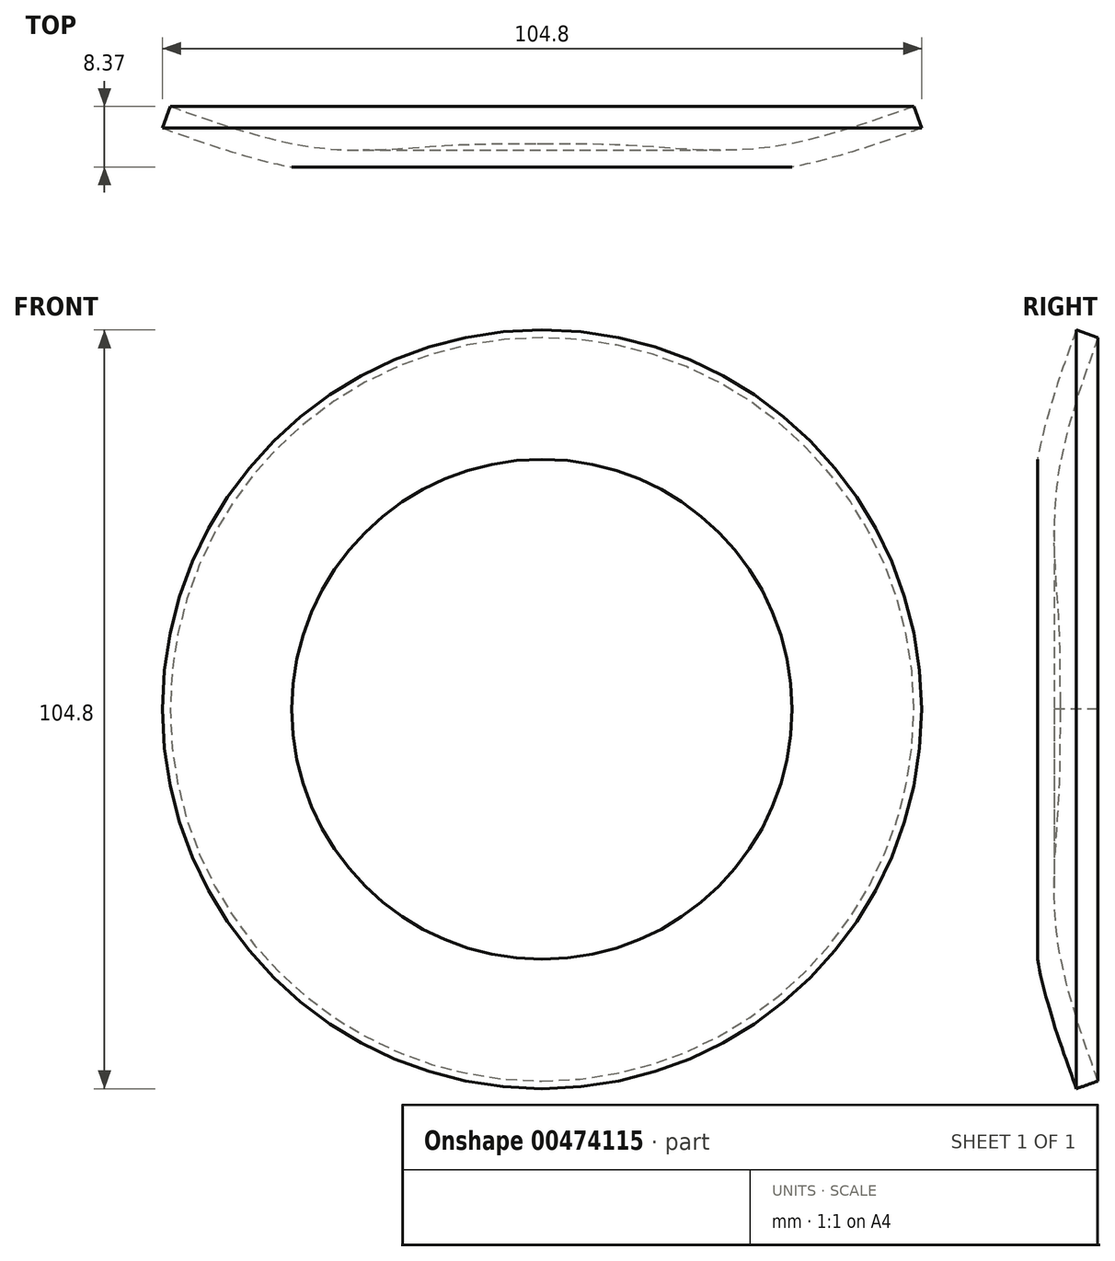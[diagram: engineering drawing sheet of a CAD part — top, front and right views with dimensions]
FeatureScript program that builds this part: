
annotation { "Feature Type Name" : "Feature", "Feature Type Description" : "" }
export const myFeature = defineFeature(function(context is Context, id is Id, definition is map)
    precondition{}
    {
        {
            var Q0;
            Q0=qCreatedBy(makeId("Top.planeOp"),FACE);
            var sketch = newSketch(context, id + "F0", { "sketchPlane" : qUnion([Q0])});
            skLineSegment(sketch, "E0", {"start": v(-26.85, 0) * mm, "end": v(-26.85, 3.18) * mm});
            skFitSpline(sketch, "E1", {"points": [v(24.49, 8.37) * mm, v(3.65, 2.62) * mm, v(-13.57, 2.91) * mm, v(-26.85, 3.18) * mm], "startDerivative": vector(-56.48, -19.98) * mm, "endDerivative": vector(-56.26, 0) * mm});
            skFitSpline(sketch, "E2.0", {"points": [v(25.55, 5.38) * mm, v(23.2, 4.55) * mm, v(19.66, 3.29) * mm, v(14.88, 1.77) * mm, v(11.27, 0.78) * mm, v(8.23, 0.1) * mm, v(5.78, -0.31) * mm, v(3.92, -0.56) * mm, v(2.07, -0.72) * mm, v(-0.36, -0.86) * mm, v(-3.34, -0.87) * mm, v(-6.76, -0.74) * mm, v(-9.98, -0.53) * mm, v(-12.46, -0.34) * mm, v(-14.28, -0.22) * mm, v(-16.02, -0.13) * mm, v(-18.12, -0.06) * mm, v(-20.7, -0.01) * mm, v(-23.52, 0) * mm, v(-25.68, 0) * mm, v(-26.85, 0) * mm]});
            skLineSegment(sketch, "E3", {"start": v(24.49, 8.37) * mm, "end": v(25.55, 5.38) * mm});
            skSolve(sketch);
        }
        {
            var Q0;
            Q0=makeQuery(id+"F0.imprint","IMPRINT",FACE,{"disambiguationData":[TD([[makeQuery(id+"F0.imprint","IMPRINT",EDGE,{"derivedFrom":sQuery(id+"F0.wireOp",EDGE,"E0")}),-1.0]])]});
            var Q1;
            Q1=sQuery(id+"F0.wireOp",EDGE,"E0");
            revolve(context, id + "F1", {"entities" : qUnion([Q0]), "axis" : qUnion([Q1]), "revolveType" : RevolveType.FULL});
        }
        {
            var Q0;
            Q0=qCreatedBy(makeId("Front.planeOp"),FACE);
            var sketch = newSketch(context, id + "F2", { "sketchPlane" : qUnion([Q0])});
            skCircle(sketch, "E4", {"center": v(-26.85, 0) * mm, "radius": 80.63 * mm});
            skSolve(sketch);
        }
        {
            var Q0;
            Q0=makeQuery(id+"F2.imprint","IMPRINT",FACE,{"disambiguationData":[TD([[makeQuery(id+"F2.imprint","IMPRINT",EDGE,{"derivedFrom":sQuery(id+"F2.wireOp",EDGE,"E4")}),1.0]])]});
            extrude(context, id + "F3", {"entities" : qUnion([Q0]), "operationType" : NewBodyOperationType.REMOVE, "depth" : 25.4 * mm});
        }
    });
